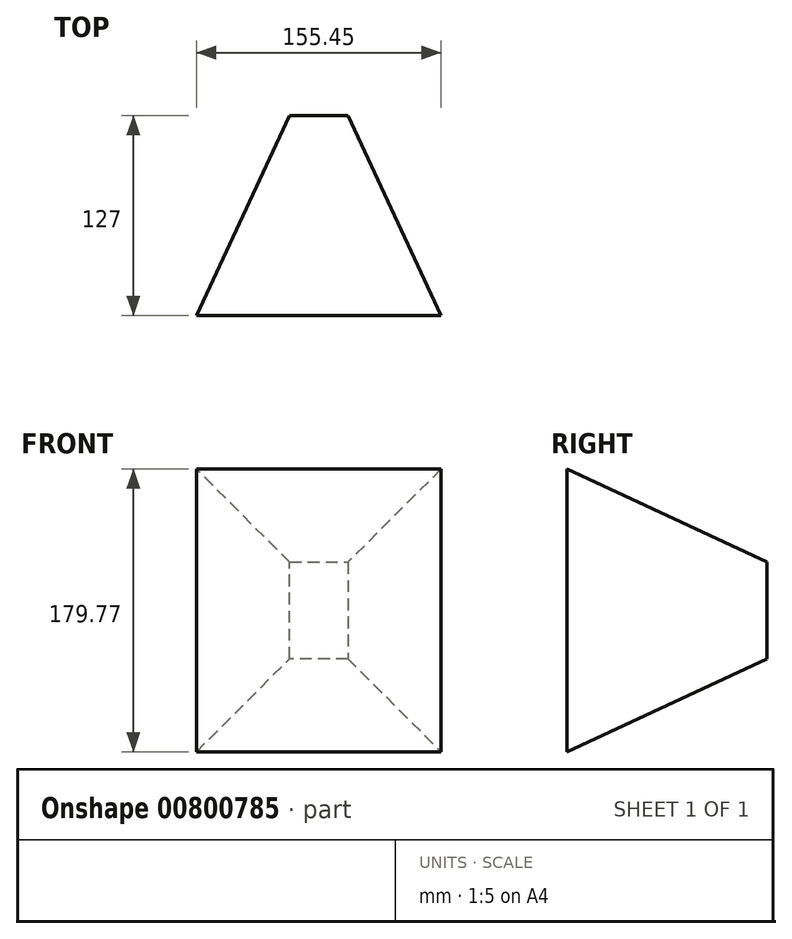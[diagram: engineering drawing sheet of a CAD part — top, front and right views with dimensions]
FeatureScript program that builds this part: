
annotation { "Feature Type Name" : "Feature", "Feature Type Description" : "" }
export const myFeature = defineFeature(function(context is Context, id is Id, definition is map)
    precondition{}
    {
        {
            var Q0;
            Q0=qCreatedBy(makeId("Front.planeOp"),FACE);
            var sketch = newSketch(context, id + "F0", { "sketchPlane" : qUnion([Q0])});
            skLineSegment(sketch, "E0.bottom", {"start": v(43, 29.23) * mm, "end": v(80.01, 29.23) * mm});
            skLineSegment(sketch, "E0.top", {"start": v(43, -32.1) * mm, "end": v(80.01, -32.1) * mm});
            skLineSegment(sketch, "E0.left", {"start": v(43, 29.23) * mm, "end": v(43, -32.1) * mm});
            skLineSegment(sketch, "E0.right", {"start": v(80.01, 29.23) * mm, "end": v(80.01, -32.1) * mm});
            skSolve(sketch);
        }
        {
            var Q0;
            Q0 = qSketchRegion(id + "F0", true);
            extrude(context, id + "F1", {"entities" : qUnion([Q0]), "depth" : 127 * mm, "offsetDistance" : 25.4 * mm, "hasDraft" : true, "draftAngle" : 25 * degree});
        }
    });
